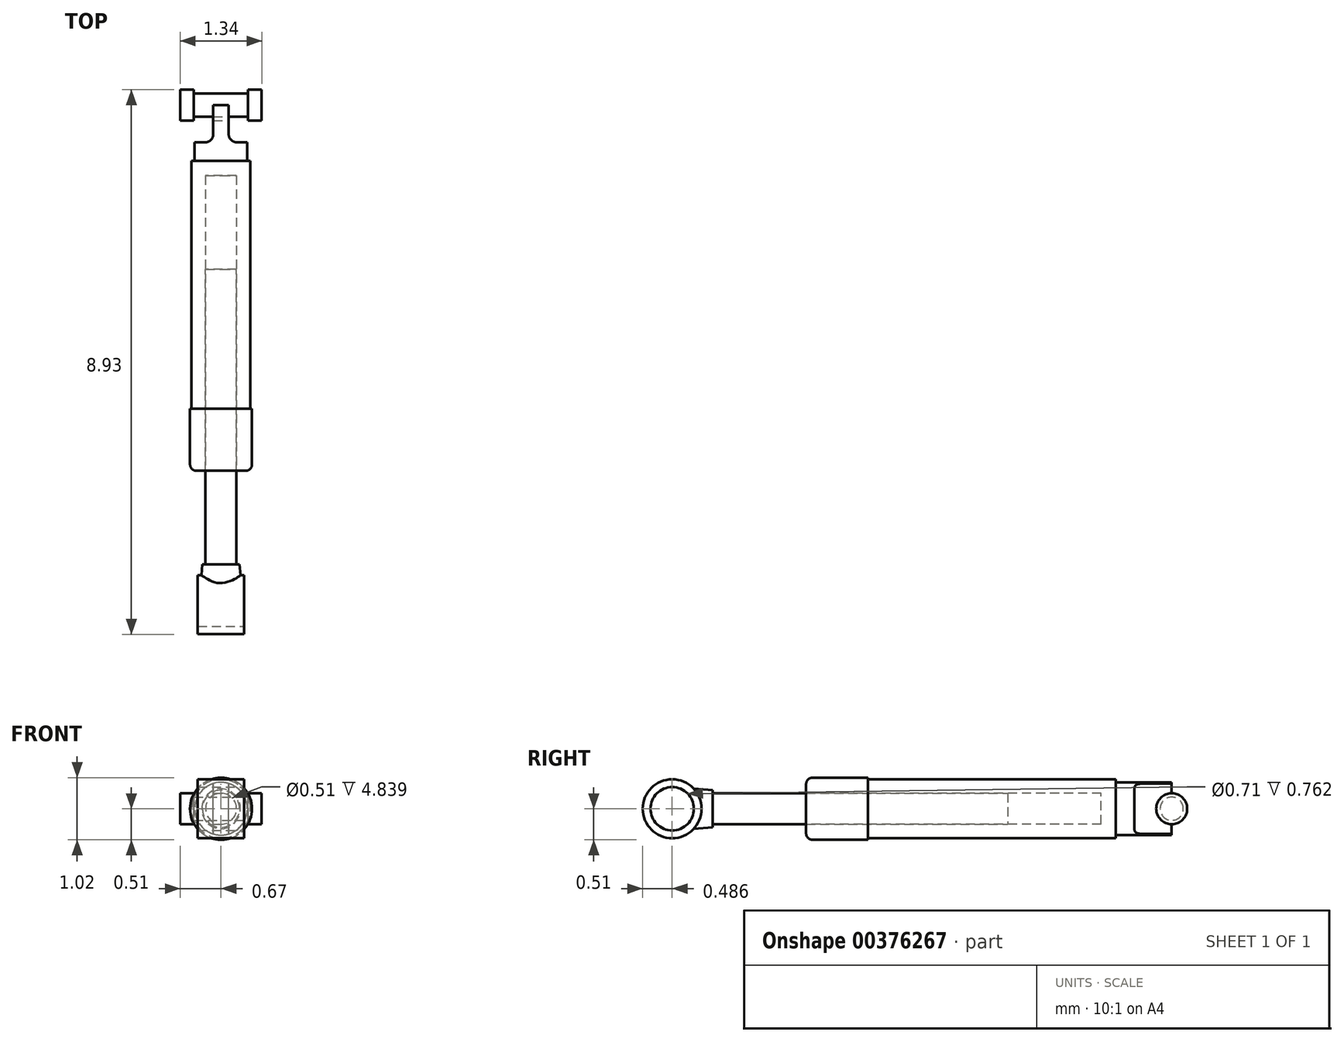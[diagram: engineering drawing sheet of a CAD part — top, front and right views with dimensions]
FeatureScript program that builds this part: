
annotation { "Feature Type Name" : "Feature", "Feature Type Description" : "" }
export const myFeature = defineFeature(function(context is Context, id is Id, definition is map)
    precondition{}
    {
        {
            var Q0;
            Q0=qCreatedBy(makeId("Right.planeOp"),FACE);
            var sketch = newSketch(context, id + "F0", { "sketchPlane" : qUnion([Q0])});
            skLineSegment(sketch, "E0", {"start": v(3.21, 0) * mm, "end": v(3.21, 0.48) * mm});
            skLineSegment(sketch, "E1", {"start": v(3.21, 0.48) * mm, "end": v(-0.85, 0.48) * mm});
            skLineSegment(sketch, "E2", {"start": v(-0.85, 0.48) * mm, "end": v(-0.85, 0.5) * mm});
            skLineSegment(sketch, "E3", {"start": v(-0.85, 0.5) * mm, "end": v(-1.87, 0.5) * mm});
            skLineSegment(sketch, "E4", {"start": v(-1.87, 0.5) * mm, "end": v(-1.87, 0.25) * mm});
            skLineSegment(sketch, "E5", {"start": v(-1.87, 0.25) * mm, "end": v(2.97, 0.25) * mm});
            skLineSegment(sketch, "E6", {"start": v(2.97, 0.25) * mm, "end": v(2.97, 0) * mm});
            skLineSegment(sketch, "E7", {"start": v(2.97, 0) * mm, "end": v(3.21, 0) * mm});
            skLineSegment(sketch, "E8", {"start": v(3.21, 0) * mm, "end": v(4.13, 0) * mm});
            skLineSegment(sketch, "E9", {"start": v(4.13, 0) * mm, "end": v(4.13, 0.43) * mm});
            skLineSegment(sketch, "E10", {"start": v(4.13, 0.43) * mm, "end": v(3.21, 0.43) * mm});
            skArc(sketch, "E11", {"start": v(4.13, 0.43) * mm, "mid": v(4.43, 0.3) * mm, "end": v(4.56, 0) * mm});
            skLineSegment(sketch, "E12", {"start": v(4.56, 0) * mm, "end": v(4.13, 0) * mm});
            skCircle(sketch, "E13", {"center": v(4.13, 0) * mm, "radius": 0.2 * mm});
            skSolve(sketch);
        }
        {
            var Q0;
            Q0=makeQuery(id+"F0.imprint","IMPRINT",FACE,{"disambiguationData":[TD([[makeQuery(id+"F0.imprint","IMPRINT",EDGE,{"derivedFrom":sQuery(id+"F0.wireOp",EDGE,"E0")}),1.0]])]});
            var Q1;
            {var subQ0=sQuery(id+"F0.wireOp",EDGE,"E8");Q1=makeQuery(id+"F0.imprint","IMPRINT",FACE,{"disambiguationData":[TD([[makeQuery(id+"F0.imprint","IMPRINT",EDGE,{"derivedFrom":subQ0}),1.0]])]});}
            var Q2;
            Q2=makeQuery(id+"F0.imprint","IMPRINT",FACE,{"disambiguationData":[TD([[makeQuery(id+"F0.imprint","IMPRINT",EDGE,{"derivedFrom":sQuery(id+"F0.wireOp",EDGE,"E9")}),-1.0]])]});
            var Q3;
            {var subQ0=sQuery(id+"F0.wireOp",EDGE,"E10");Q3=makeQuery(id+"F0.imprint","IMPRINT",FACE,{"disambiguationData":[TD([[makeQuery(id+"F0.imprint","IMPRINT",EDGE,{"derivedFrom":subQ0}),1.0]])]});}
            var Q4;
            {var subQ0=sQuery(id+"F0.wireOp",EDGE,"E11");Q4=makeQuery(id+"F0.imprint","IMPRINT",FACE,{"disambiguationData":[TD([[makeQuery(id+"F0.imprint","IMPRINT",EDGE,{"derivedFrom":subQ0}),-1.0]])]});}
            var Q5;
            Q5=sQuery(id+"F0.wireOp",EDGE,"E7");
            revolve(context, id + "F1", {"entities" : qUnion([Q0, Q1, Q2, Q3, Q4]), "axis" : qUnion([Q5]), "revolveType" : RevolveType.FULL});
        }
        {
            var Q0;
            Q0=makeQuery(id+"F1.opRevolve","SWEPT_EDGE",EDGE,{"disambiguationData":[OSD([sQuery(id+"F0.wireOp",EDGE,"E3"),sQuery(id+"F0.wireOp",EDGE,"E4")])]});
            fillet(context, id + "F2", {"entities" : qUnion([Q0]), "radius" : 0.1 * mm, "tangentPropagation" : true, "allowEdgeOverflow" : false});
        }
        {
            var Q0;
            Q0=qCreatedBy(makeId("Top.planeOp"),FACE);
            var sketch = newSketch(context, id + "F3", { "sketchPlane" : qUnion([Q0])});
            skLineSegment(sketch, "E14", {"start": v(0, 0) * mm, "end": v(0, 7.15) * mm, "construction": true});
            skLineSegment(sketch, "E15.bottom", {"start": v(0.13, 4.79) * mm, "end": v(0.64, 4.79) * mm});
            skLineSegment(sketch, "E15.top", {"start": v(0.13, 3.52) * mm, "end": v(0.64, 3.52) * mm});
            skLineSegment(sketch, "E15.left", {"start": v(0.13, 4.79) * mm, "end": v(0.13, 3.52) * mm});
            skLineSegment(sketch, "E15.right", {"start": v(0.64, 4.79) * mm, "end": v(0.64, 3.52) * mm});
            skLineSegment(sketch, "E16.MirrorCS", {"start": v(-0.13, 4.79) * mm, "end": v(-0.13, 3.52) * mm});
            skLineSegment(sketch, "E17.MirrorCS", {"start": v(-0.13, 3.52) * mm, "end": v(-0.64, 3.52) * mm});
            skLineSegment(sketch, "E18.MirrorCS", {"start": v(-0.64, 4.79) * mm, "end": v(-0.64, 3.52) * mm});
            skLineSegment(sketch, "E19.MirrorCS", {"start": v(-0.13, 4.79) * mm, "end": v(-0.64, 4.79) * mm});
            skSolve(sketch);
        }
        {
            var Q0;
            Q0=makeQuery(id+"F3.imprint","IMPRINT",FACE,{"disambiguationData":[TD([[makeQuery(id+"F3.imprint","IMPRINT",EDGE,{"derivedFrom":sQuery(id+"F3.wireOp",EDGE,"E16.MirrorCS")}),-1.0]])]});
            var Q1;
            Q1=makeQuery(id+"F3.imprint","IMPRINT",FACE,{"disambiguationData":[TD([[makeQuery(id+"F3.imprint","IMPRINT",EDGE,{"derivedFrom":sQuery(id+"F3.wireOp",EDGE,"E15.bottom")}),-1.0]])]});
            extrude(context, id + "F4", {"entities" : qUnion([Q0, Q1]), "operationType" : NewBodyOperationType.REMOVE, "endBound" : BoundingType.SYMMETRIC, "oppositeDirection" : true, "depth" : 2.54 * mm});
        }
        {
            var Q0;
            Q0=makeQuery(id+"F4.boolean.opBoolean","COPY",EDGE,{"derivedFrom":makeQuery(id+"F4.opExtrude","SWEPT_EDGE",EDGE,{"disambiguationData":[OSD([sQuery(id+"F3.wireOp",EDGE,"E16.MirrorCS"),sQuery(id+"F3.wireOp",EDGE,"E17.MirrorCS")])]})});
            var Q1;
            Q1=makeQuery(id+"F4.boolean.opBoolean","COPY",EDGE,{"derivedFrom":makeQuery(id+"F4.opExtrude","SWEPT_EDGE",EDGE,{"disambiguationData":[OSD([sQuery(id+"F3.wireOp",EDGE,"E15.top"),sQuery(id+"F3.wireOp",EDGE,"E15.left")])]})});
            fillet(context, id + "F5", {"entities" : qUnion([Q0, Q1]), "radius" : 0.13 * mm, "tangentPropagation" : true, "allowEdgeOverflow" : false});
        }
        {
            var Q0;
            {var subQ0=sQuery(id+"F0.wireOp",EDGE,"E12");var subQ3=sQuery(id+"F0.wireOp",EDGE,"E13");var subQ5=makeQuery(id+"F0.imprint","INTERSECT",VERTEX,{"derivedFrom":[subQ0,subQ3]});Q0=makeQuery(id+"F0.imprint","IMPRINT",FACE,{"disambiguationData":[TD([[makeQuery(id+"F0.imprint","IMPRINT",EDGE,{"disambiguationData":[TD([[subQ5,-1.0]])],"derivedFrom":subQ3}),1.0]])]});}
            var Q1;
            {var subQ1=sQuery(id+"F0.wireOp",EDGE,"E8");var subQ3=sQuery(id+"F0.wireOp",EDGE,"E13");var subQ4=makeQuery(id+"F0.imprint","INTERSECT",VERTEX,{"derivedFrom":[subQ1,subQ3]});Q1=makeQuery(id+"F0.imprint","IMPRINT",FACE,{"disambiguationData":[TD([[makeQuery(id+"F0.imprint","IMPRINT",EDGE,{"disambiguationData":[TD([[subQ4,1.0]])],"derivedFrom":subQ3}),1.0]])]});}
            var Q2;
            {var subQ1=sQuery(id+"F0.wireOp",EDGE,"E8");var subQ3=sQuery(id+"F0.wireOp",EDGE,"E13");var subQ4=makeQuery(id+"F0.imprint","INTERSECT",VERTEX,{"derivedFrom":[subQ1,subQ3]});Q2=makeQuery(id+"F0.imprint","IMPRINT",FACE,{"disambiguationData":[TD([[makeQuery(id+"F0.imprint","IMPRINT",EDGE,{"disambiguationData":[TD([[subQ4,-1.0]])],"derivedFrom":subQ3}),1.0]])]});}
            extrude(context, id + "F6", {"entities" : qUnion([Q0, Q1, Q2]), "operationType" : NewBodyOperationType.REMOVE, "endBound" : BoundingType.SYMMETRIC, "oppositeDirection" : true, "depth" : 25.4 * mm});
        }
        {
            var Q0;
            Q0=qCreatedBy(makeId("Right.planeOp"),FACE);
            var sketch = newSketch(context, id + "F7", { "sketchPlane" : qUnion([Q0])});
            skCircle(sketch, "E20", {"center": v(-4.06, 0) * mm, "radius": 0.48 * mm});
            skLineSegment(sketch, "E21.bottom", {"start": v(1.44, 0) * mm, "end": v(-3.4, 0) * mm});
            skLineSegment(sketch, "E21.top", {"start": v(1.44, 0.25) * mm, "end": v(-3.4, 0.25) * mm});
            skLineSegment(sketch, "E21.left", {"start": v(1.44, 0) * mm, "end": v(1.44, 0.25) * mm});
            skLineSegment(sketch, "E21.right", {"start": v(-3.4, 0) * mm, "end": v(-3.4, 0.25) * mm});
            skCircle(sketch, "E22", {"center": v(-4.06, 0) * mm, "radius": 0.36 * mm});
            skLineSegment(sketch, "E23", {"start": v(-3.4, 0.25) * mm, "end": v(-3.4, 0.3) * mm});
            skLineSegment(sketch, "E24", {"start": v(-3.4, 0.3) * mm, "end": v(-4.04, 0.35) * mm});
            skLineSegment(sketch, "E25", {"start": v(-3.4, 0) * mm, "end": v(-3.7, 0) * mm});
            skSolve(sketch);
        }
        {
            var Q0;
            {var subQ0=sQuery(id+"F7.wireOp",EDGE,"E22");var subQ1=makeQuery(id+"F7.imprint","INTERSECT",VERTEX,{"derivedFrom":[subQ0,sQuery(id+"F7.wireOp",EDGE,"E24")]});Q0=makeQuery(id+"F7.imprint","IMPRINT",FACE,{"disambiguationData":[TD([[makeQuery(id+"F7.imprint","IMPRINT",EDGE,{"disambiguationData":[TD([[subQ1,1.0]])],"derivedFrom":subQ0}),1.0]])]});}
            var Q1;
            {var subQ0=sQuery(id+"F7.wireOp",EDGE,"E24");var subQ1=sQuery(id+"F7.wireOp",EDGE,"E20");var subQ2=makeQuery(id+"F7.imprint","INTERSECT",VERTEX,{"derivedFrom":[subQ1,subQ0]});Q1=makeQuery(id+"F7.imprint","IMPRINT",FACE,{"disambiguationData":[TD([[makeQuery(id+"F7.imprint","IMPRINT",EDGE,{"disambiguationData":[TD([[subQ2,1.0]])],"derivedFrom":subQ1}),1.0]])]});}
            var Q2;
            {var subQ0=sQuery(id+"F7.wireOp",EDGE,"E24");var subQ1=sQuery(id+"F7.wireOp",EDGE,"E20");var subQ2=makeQuery(id+"F7.imprint","INTERSECT",VERTEX,{"derivedFrom":[subQ1,subQ0]});Q2=makeQuery(id+"F7.imprint","IMPRINT",FACE,{"disambiguationData":[TD([[makeQuery(id+"F7.imprint","IMPRINT",EDGE,{"disambiguationData":[TD([[subQ2,-1.0]])],"derivedFrom":subQ1}),1.0]])]});}
            extrude(context, id + "F8", {"entities" : qUnion([Q0, Q1, Q2]), "endBound" : BoundingType.SYMMETRIC, "depth" : 0.76 * mm});
        }
        {
            var Q0;
            {var subQ6=sQuery(id+"F7.wireOp",EDGE,"E21.right");Q0=makeQuery(id+"F7.imprint","IMPRINT",FACE,{"disambiguationData":[TD([[makeQuery(id+"F7.imprint","IMPRINT",EDGE,{"derivedFrom":subQ6}),1.0]])]});}
            var Q1;
            {var subQ0=sQuery(id+"F7.wireOp",EDGE,"E24");var subQ1=sQuery(id+"F7.wireOp",EDGE,"E20");var subQ2=makeQuery(id+"F7.imprint","INTERSECT",VERTEX,{"derivedFrom":[subQ1,subQ0]});Q1=makeQuery(id+"F7.imprint","IMPRINT",FACE,{"disambiguationData":[TD([[makeQuery(id+"F7.imprint","IMPRINT",EDGE,{"disambiguationData":[TD([[subQ2,1.0]])],"derivedFrom":subQ1}),1.0]])]});}
            var Q2;
            Q2=sQuery(id+"F7.wireOp",EDGE,"E25");
            revolve(context, id + "F9", {"operationType" : NewBodyOperationType.ADD, "entities" : qUnion([Q0, Q1]), "axis" : qUnion([Q2]), "revolveType" : RevolveType.FULL});
        }
        {
            var Q0;
            {var subQ0=sQuery(id+"F7.wireOp",EDGE,"E22");var subQ1=makeQuery(id+"F7.imprint","INTERSECT",VERTEX,{"derivedFrom":[subQ0,sQuery(id+"F7.wireOp",EDGE,"E24")]});Q0=makeQuery(id+"F7.imprint","IMPRINT",FACE,{"disambiguationData":[TD([[makeQuery(id+"F7.imprint","IMPRINT",EDGE,{"disambiguationData":[TD([[subQ1,1.0]])],"derivedFrom":subQ0}),1.0]])]});}
            extrude(context, id + "F10", {"entities" : qUnion([Q0]), "operationType" : NewBodyOperationType.REMOVE, "endBound" : BoundingType.SYMMETRIC, "oppositeDirection" : true, "depth" : 25.4 * mm});
        }
        {
            var Q0;
            Q0=makeQuery(id+"F7.imprint","IMPRINT",FACE,{"disambiguationData":[TD([[makeQuery(id+"F7.imprint","IMPRINT",EDGE,{"derivedFrom":sQuery(id+"F7.wireOp",EDGE,"E21.bottom")}),-1.0]])]});
            var Q1;
            Q1=sQuery(id+"F7.wireOp",EDGE,"E21.bottom");
            revolve(context, id + "F11", {"entities" : qUnion([Q0]), "axis" : qUnion([Q1]), "revolveType" : RevolveType.FULL});
        }
        {
            var Q0;
            Q0=qCreatedBy(makeId("Right.planeOp"),FACE);
            var sketch = newSketch(context, id + "F12", { "sketchPlane" : qUnion([Q0])});
            skCircle(sketch, "E26.0", {"center": v(4.13, 0) * mm, "radius": 0.2 * mm});
            skCircle(sketch, "E27", {"center": v(4.13, 0) * mm, "radius": 0.25 * mm});
            skSolve(sketch);
        }
        {
            var Q0;
            Q0=makeQuery(id+"F12.imprint","IMPRINT",FACE,{"disambiguationData":[TD([[makeQuery(id+"F12.imprint","IMPRINT",EDGE,{"derivedFrom":sQuery(id+"F12.wireOp",EDGE,"E26.0")}),1.0]])]});
            var Q1;
            Q1=makeQuery(id+"F12.imprint","IMPRINT",FACE,{"disambiguationData":[TD([[makeQuery(id+"F12.imprint","IMPRINT",EDGE,{"derivedFrom":sQuery(id+"F12.wireOp",EDGE,"E26.0")}),-1.0]])]});
            extrude(context, id + "F13", {"entities" : qUnion([Q0, Q1]), "endBound" : BoundingType.SYMMETRIC, "depth" : 1.33 * mm});
        }
        {
            var Q0;
            Q0=makeQuery(id+"F12.imprint","IMPRINT",FACE,{"disambiguationData":[TD([[makeQuery(id+"F12.imprint","IMPRINT",EDGE,{"derivedFrom":sQuery(id+"F12.wireOp",EDGE,"E26.0")}),-1.0]])]});
            extrude(context, id + "F14", {"entities" : qUnion([Q0]), "operationType" : NewBodyOperationType.REMOVE, "endBound" : BoundingType.SYMMETRIC, "oppositeDirection" : true, "depth" : 0.89 * mm});
        }
    });
